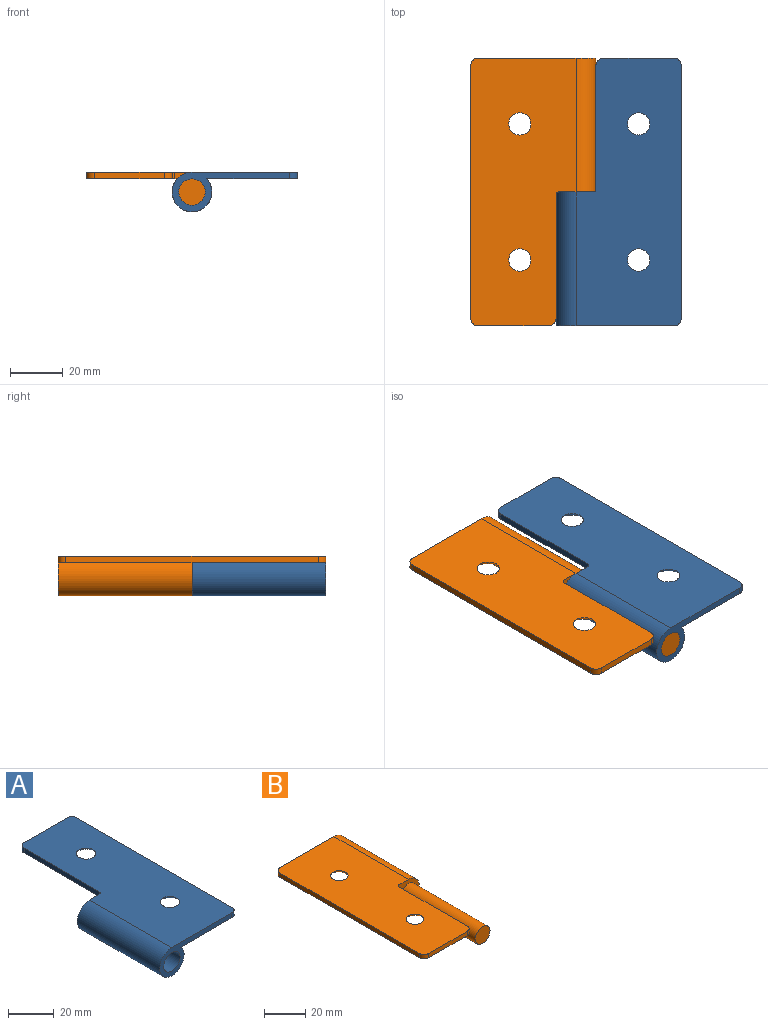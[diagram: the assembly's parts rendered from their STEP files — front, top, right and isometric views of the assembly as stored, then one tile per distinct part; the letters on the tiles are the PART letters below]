
ASSEMBLY  parts=2 mates=1
PART A: 15 faces, bbox 47.5x101.6x15 mm
  f0: plane 15x15mm, normal (0,1,0), area 104.7mm2, adj f1,f2,f4,f5,f9
  f1: cylinder r=7.5mm len=50.8mm, axis (0,1,0), area 2073.4mm2, adj f0,f2,f5,f6
  f2: plane 101.6x34.41mm, normal (0,0,-1), area 3109.7mm2, adj f0,f1,f3,f6,f7,f8,f9,f10
  f3: plane 95.6x2.5mm, normal (1,0,0), area 239mm2, adj f2,f5,f10,f12
  f4: cylinder r=5mm len=50.8mm, axis (0,1,0), area 1595.9mm2, adj f0,f6
  f5: plane 101.6x40mm, normal (0,0,1), area 3565.5mm2, adj f0,f1,f3,f6,f7,f8,f9,f10
  f6: plane 44.5x15mm, normal (0,-1,0), area 181mm2, adj f1,f2,f4,f5,f12
  f7: plane 26.5x2.5mm, normal (0,1,0), area 66.2mm2, adj f2,f5,f10,f11
  f8: plane 46.8x2.5mm, normal (-1,0,0), area 117mm2, adj f2,f5,f9,f11
  f9: cylinder r=1mm len=2.5mm, axis (0,0,-1), area 3.9mm2, adj f0,f2,f5,f8
  f10: cylinder r=3mm len=3mm, axis (0,0,-1), area 11.8mm2, adj f2,f3,f5,f7
  f11: cylinder r=3mm len=3mm, axis (0,0,-1), area 11.8mm2, adj f2,f5,f7,f8
  f12: cylinder r=3mm len=3mm, axis (0,0,-1), area 11.8mm2, adj f2,f3,f5,f6
  f13: cone r=3.3mm half-angle=45deg, axis (0,0,-1), area 121.5mm2, adj f2,f5
  f14: cone r=3.3mm half-angle=45deg, axis (0,0,-1), area 121.5mm2, adj f2,f5
PART B: 16 faces, bbox 47.5x101.6x15 mm
  f0: plane 95.6x2.5mm, normal (-1,0,0), area 239mm2, adj f1,f3,f11,f12
  f1: plane 101.6x34.41mm, normal (0,0,-1), area 3109.7mm2, adj f0,f2,f4,f5,f8,f9,f10,f11
  f2: cylinder r=7.5mm len=50.8mm, axis (0,-1,0), area 2073.4mm2, adj f1,f3,f4,f5
  f3: plane 101.6x40mm, normal (0,0,1), area 3565.5mm2, adj f0,f2,f4,f5,f8,f9,f10,f11
  f4: plane 44.5x15mm, normal (0,1,0), area 259.5mm2, adj f1,f2,f3,f12
  f5: plane 15x15mm, normal (0,-1,0), area 104.7mm2, adj f1,f2,f3,f6,f13
  f6: cylinder r=5mm len=50.8mm, axis (0,1,0), area 1595.9mm2, adj f5,f7
  f7: plane 10x10mm, normal (0,-1,0), area 78.5mm2, adj f6
  f8: plane 26.5x2.5mm, normal (0,-1,0), area 66.2mm2, adj f1,f3,f10,f11
  f9: plane 46.8x2.5mm, normal (1,0,0), area 117mm2, adj f1,f3,f10,f13
  f10: cylinder r=3mm len=3mm, axis (0,0,-1), area 11.8mm2, adj f1,f3,f8,f9
  f11: cylinder r=3mm len=3mm, axis (0,0,-1), area 11.8mm2, adj f0,f1,f3,f8
  f12: cylinder r=3mm len=3mm, axis (0,0,1), area 11.8mm2, adj f0,f1,f3,f4
  f13: cylinder r=1mm len=2.5mm, axis (0,0,1), area 3.9mm2, adj f1,f3,f5,f9
  f14: cone r=3.3mm half-angle=45deg, axis (0,0,-1), area 121.5mm2, adj f1,f3
  f15: cone r=3.3mm half-angle=45deg, axis (0,0,-1), area 121.5mm2, adj f1,f3
PLACE A t=(0,-90.1,0)mm fixed
PLACE B t=(0,-90.1,0)mm
MATE revolute B.f6 <-> A.f4  axis (0,-1,0) through (0,-140.9,0)mm
